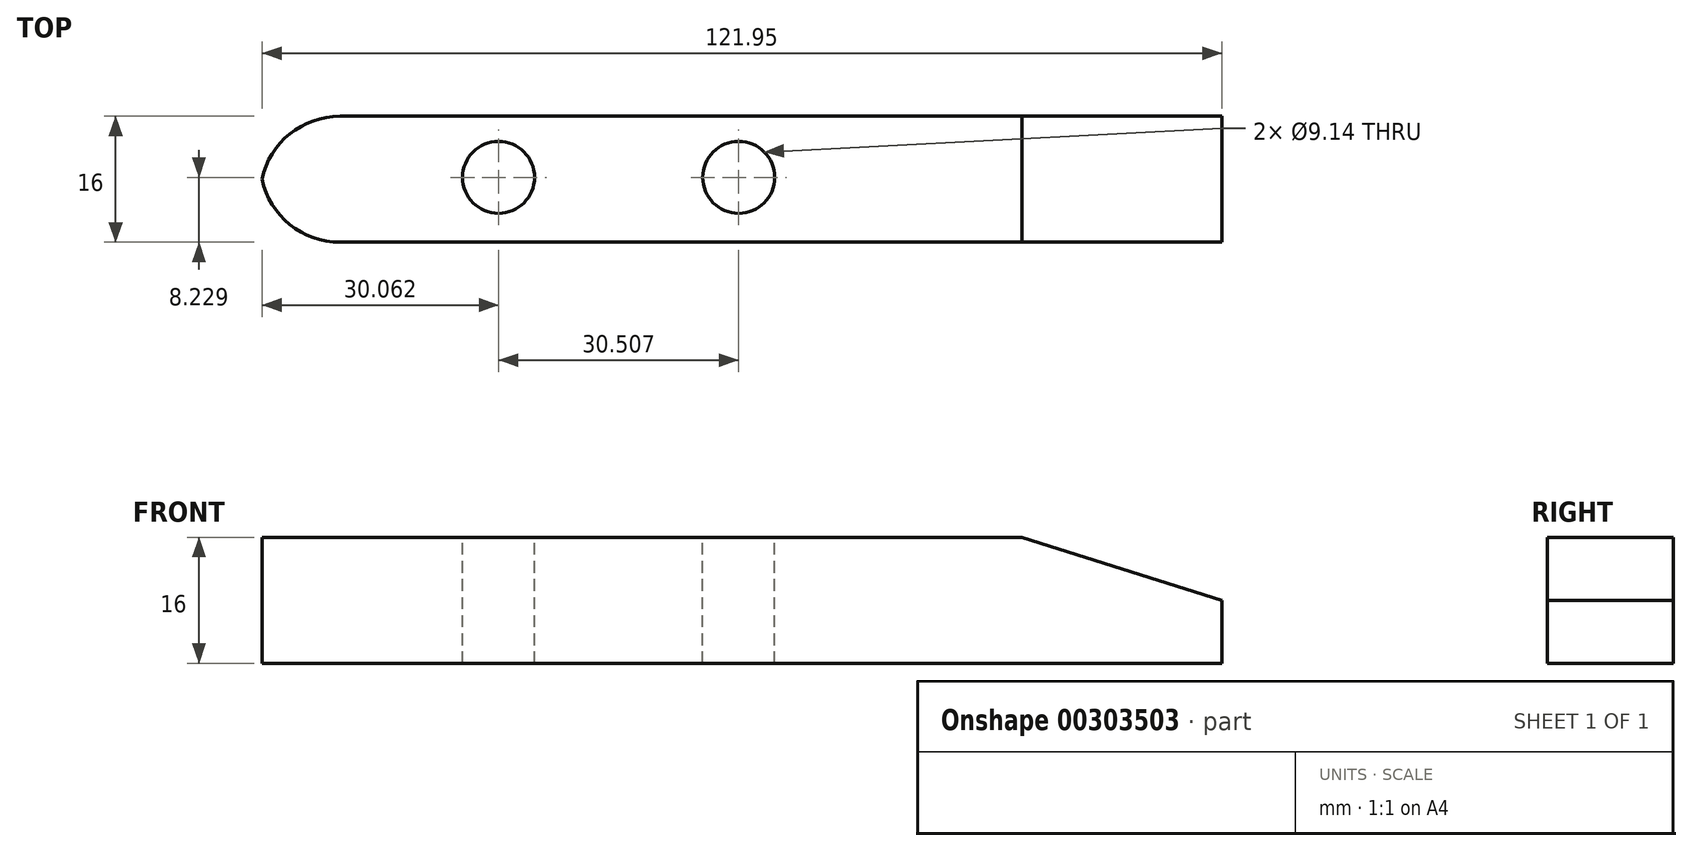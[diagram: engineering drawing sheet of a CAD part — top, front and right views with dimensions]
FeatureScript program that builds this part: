
annotation { "Feature Type Name" : "Feature", "Feature Type Description" : "" }
export const myFeature = defineFeature(function(context is Context, id is Id, definition is map)
    precondition{}
    {
        {
            var Q0;
            Q0=qCreatedBy(makeId("Front.planeOp"),FACE);
            var sketch = newSketch(context, id + "F0", { "sketchPlane" : qUnion([Q0])});
            skLineSegment(sketch, "E0.bottom", {"start": v(-37.92, 9.87) * mm, "end": v(58.86, 9.87) * mm});
            skLineSegment(sketch, "E0.top", {"start": v(-37.92, -6.13) * mm, "end": v(84.26, -6.13) * mm});
            skLineSegment(sketch, "E0.left", {"start": v(-37.92, 9.87) * mm, "end": v(-37.92, -6.13) * mm});
            skLineSegment(sketch, "E1", {"start": v(58.86, 9.87) * mm, "end": v(84.26, 1.87) * mm});
            skPoint(sketch, "E2.orphan", {"position": v(84.26, 9.87) * mm});
            skLineSegment(sketch, "E3", {"start": v(84.26, 1.87) * mm, "end": v(84.26, -6.13) * mm});
            skSolve(sketch);
        }
        {
            var Q0;
            Q0=makeQuery(id+"F0.imprint","IMPRINT",FACE,{"disambiguationData":[TD([[makeQuery(id+"F0.imprint","IMPRINT",EDGE,{"derivedFrom":sQuery(id+"F0.wireOp",EDGE,"E0.bottom")}),-1.0]])]});
            extrude(context, id + "F1", {"entities" : qUnion([Q0]), "depth" : 16 * mm});
        }
        {
            var Q0;
            Q0=makeQuery(id+"F1.opExtrude","SWEPT_FACE",FACE,{"disambiguationData":[OSD([sQuery(id+"F0.wireOp",EDGE,"E0.bottom")])]});
            var sketch = newSketch(context, id + "F2", { "sketchPlane" : qUnion([Q0])});
            skPoint(sketch, "E4", {"position": v(-7.63, -7.77) * mm});
            skPoint(sketch, "E5", {"position": v(22.88, -7.77) * mm});
            skSolve(sketch);
        }
        {
            var Q0;
            Q0=sQuery(id+"F2.wireOp",VERTEX,"E4");
            var Q1;
            Q1=sQuery(id+"F2.wireOp",VERTEX,"E5");
            var Q2;
            Q2=makeQuery(id+"F1.opExtrude","SWEPT_BODY",BODY,{"disambiguationData":[OSD([sQuery(id+"F0.wireOp",EDGE,"E0.bottom"),sQuery(id+"F0.wireOp",EDGE,"E0.top"),sQuery(id+"F0.wireOp",EDGE,"E0.left"),sQuery(id+"F0.wireOp",EDGE,"E1"),sQuery(id+"F0.wireOp",EDGE,"E3")])]});
            hole(context, id + "F3", {"style" : HoleStyle.SIMPLE, "endStyle" : HoleEndStyle.THROUGH, "holeDiameter" : 9.14 * mm, "tappedDepth" : 12.7 * mm, "tapClearance" : 3, "locations" : qUnion([Q0, Q1]), "scope" : qUnion([Q2])});
        }
        {
            var Q0;
            Q0=makeQuery(id+"F1.opExtrude","CAP_EDGE",EDGE,{"disambiguationData":[OSD([sQuery(id+"F0.wireOp",EDGE,"E0.left")])],"isStart":false});
            var Q1;
            Q1=makeQuery(id+"F1.opExtrude","CAP_EDGE",EDGE,{"disambiguationData":[OSD([sQuery(id+"F0.wireOp",EDGE,"E0.left")])],"isStart":true});
            fillet(context, id + "F4", {"entities" : qUnion([Q0, Q1]), "radius" : 10.16 * mm, "tangentPropagation" : true, "allowEdgeOverflow" : false});
        }
    });
